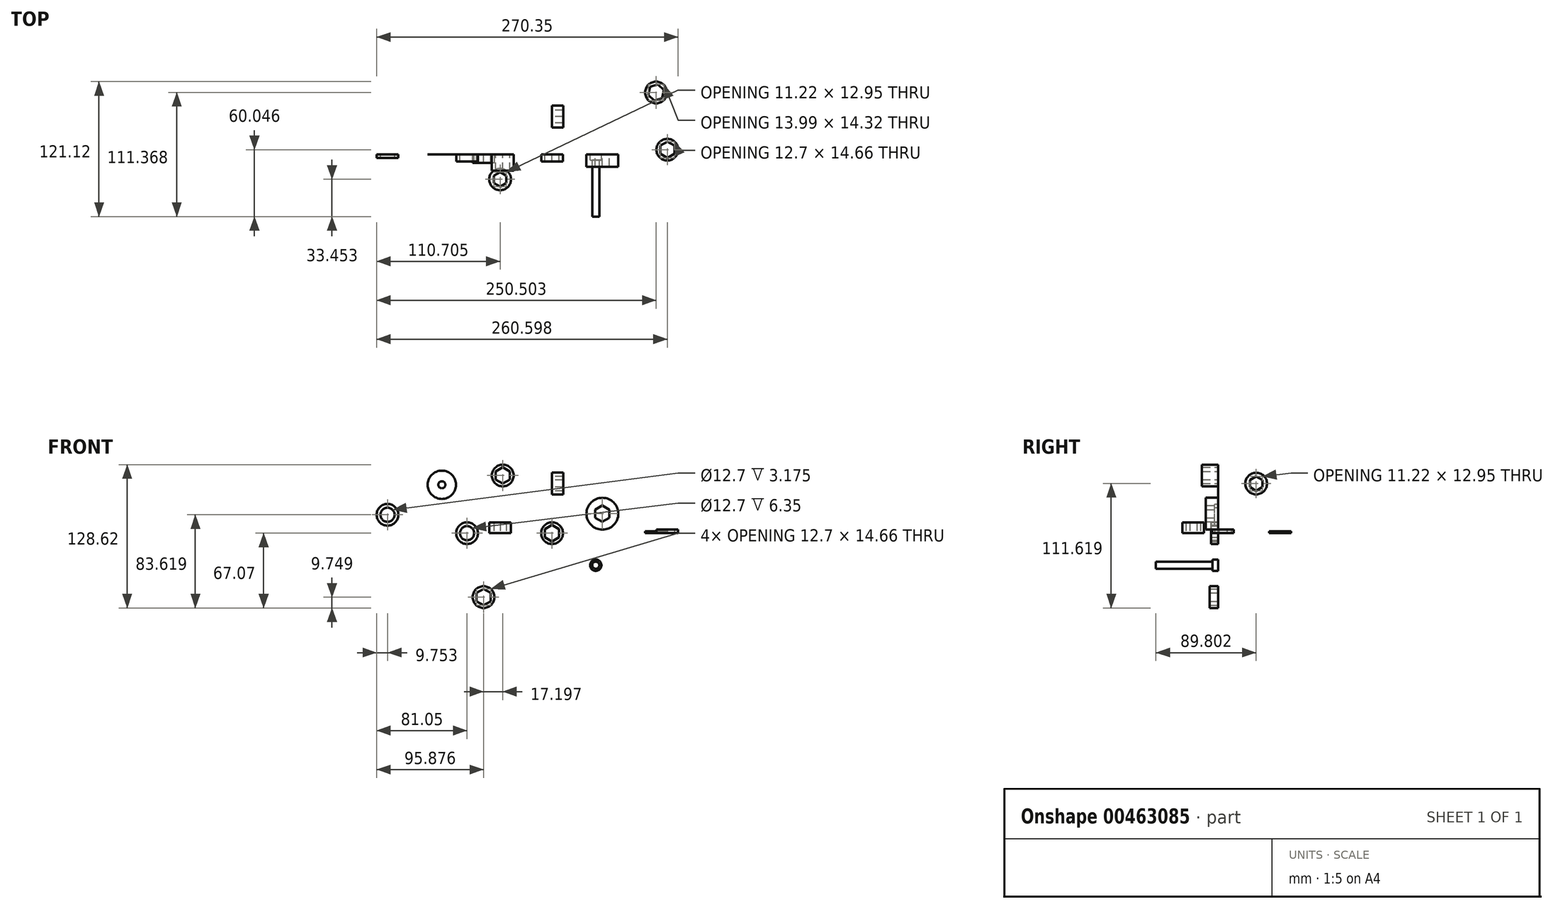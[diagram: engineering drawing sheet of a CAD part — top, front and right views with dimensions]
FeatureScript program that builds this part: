
annotation { "Feature Type Name" : "Feature", "Feature Type Description" : "" }
export const myFeature = defineFeature(function(context is Context, id is Id, definition is map)
    precondition{}
    {
        {
            var Q0;
            Q0=qCreatedBy(makeId("Front.planeOp"),FACE);
            var sketch = newSketch(context, id + "F0", { "sketchPlane" : qUnion([Q0])});
            skCircle(sketch, "E0.cCircle", {"center": v(0, 0) * mm, "radius": 7.33 * mm, "construction": true});
            skLineSegment(sketch, "E0.0", {"start": v(6.35, 3.67) * mm, "end": v(6.35, -3.67) * mm});
            skLineSegment(sketch, "E0.1", {"start": v(6.35, -3.67) * mm, "end": v(0, -7.33) * mm});
            skLineSegment(sketch, "E0.2", {"start": v(0, -7.33) * mm, "end": v(-6.35, -3.67) * mm});
            skLineSegment(sketch, "E0.3", {"start": v(-6.35, -3.67) * mm, "end": v(-6.35, 3.67) * mm});
            skLineSegment(sketch, "E0.4", {"start": v(-6.35, 3.67) * mm, "end": v(0, 7.33) * mm});
            skLineSegment(sketch, "E0.5", {"start": v(0, 7.33) * mm, "end": v(6.35, 3.67) * mm});
            skLineSegment(sketch, "E1", {"start": v(0, 0) * mm, "end": v(0, 7.33) * mm, "construction": true});
            skCircle(sketch, "E2", {"center": v(0, 0) * mm, "radius": 9.75 * mm});
            skLineSegment(sketch, "E3", {"start": v(0, 0) * mm, "end": v(-3.18, 5.5) * mm, "construction": true});
            skSolve(sketch);
        }
        {
            var Q0;
            Q0=makeQuery(id+"F0.imprint","IMPRINT",FACE,{"disambiguationData":[TD([[makeQuery(id+"F0.imprint","IMPRINT",EDGE,{"derivedFrom":sQuery(id+"F0.wireOp",EDGE,"E0.0")}),1.0]])]});
            extrude(context, id + "F1", {"entities" : qUnion([Q0]), "depth" : 6.35 * mm});
        }
        {
            var Q0;
            Q0=qCreatedBy(makeId("Top.planeOp"),FACE);
            var sketch = newSketch(context, id + "F2", { "sketchPlane" : qUnion([Q0])});
            skCircle(sketch, "E4.cCircle", {"center": v(-46.55, -22.43) * mm, "radius": 6.48 * mm, "construction": true});
            skLineSegment(sketch, "E4.0", {"start": v(-40.94, -19.19) * mm, "end": v(-40.94, -25.67) * mm});
            skLineSegment(sketch, "E4.1", {"start": v(-40.94, -25.67) * mm, "end": v(-46.55, -28.9) * mm});
            skLineSegment(sketch, "E4.2", {"start": v(-46.55, -28.9) * mm, "end": v(-52.15, -25.67) * mm});
            skLineSegment(sketch, "E4.3", {"start": v(-52.15, -25.67) * mm, "end": v(-52.15, -19.19) * mm});
            skLineSegment(sketch, "E4.4", {"start": v(-52.15, -19.19) * mm, "end": v(-46.55, -15.95) * mm});
            skLineSegment(sketch, "E4.5", {"start": v(-46.55, -15.95) * mm, "end": v(-40.94, -19.19) * mm});
            skLineSegment(sketch, "E5", {"start": v(-46.55, -22.43) * mm, "end": v(-46.55, -15.95) * mm, "construction": true});
            skCircle(sketch, "E6", {"center": v(-46.55, -22.43) * mm, "radius": 9.75 * mm});
            skSolve(sketch);
        }
        {
            var Q0;
            Q0=makeQuery(id+"F2.imprint","IMPRINT",FACE,{"disambiguationData":[TD([[makeQuery(id+"F2.imprint","IMPRINT",EDGE,{"derivedFrom":sQuery(id+"F2.wireOp",EDGE,"E4.0")}),1.0]])]});
            extrude(context, id + "F3", {"entities" : qUnion([Q0]), "depth" : 9.52 * mm});
        }
        {
            var Q0;
            Q0=qCreatedBy(makeId("Right.planeOp"),FACE);
            var sketch = newSketch(context, id + "F4", { "sketchPlane" : qUnion([Q0])});
            skCircle(sketch, "E7.cCircle", {"center": v(33.92, 44.55) * mm, "radius": 6.48 * mm, "construction": true});
            skLineSegment(sketch, "E7.0", {"start": v(39.53, 47.79) * mm, "end": v(39.53, 41.31) * mm});
            skLineSegment(sketch, "E7.1", {"start": v(39.53, 41.31) * mm, "end": v(33.92, 38.07) * mm});
            skLineSegment(sketch, "E7.2", {"start": v(33.92, 38.07) * mm, "end": v(28.31, 41.31) * mm});
            skLineSegment(sketch, "E7.3", {"start": v(28.31, 41.31) * mm, "end": v(28.31, 47.79) * mm});
            skLineSegment(sketch, "E7.4", {"start": v(28.31, 47.79) * mm, "end": v(33.92, 51.03) * mm});
            skLineSegment(sketch, "E7.5", {"start": v(33.92, 51.03) * mm, "end": v(39.53, 47.79) * mm});
            skLineSegment(sketch, "E8", {"start": v(33.92, 44.55) * mm, "end": v(33.92, 51.03) * mm, "construction": true});
            skCircle(sketch, "E9", {"center": v(33.92, 44.55) * mm, "radius": 9.75 * mm});
            skSolve(sketch);
        }
        {
            var Q0;
            Q0=makeQuery(id+"F4.imprint","IMPRINT",FACE,{"disambiguationData":[TD([[makeQuery(id+"F4.imprint","IMPRINT",EDGE,{"derivedFrom":sQuery(id+"F4.wireOp",EDGE,"E7.0")}),1.0]])]});
            extrude(context, id + "F5", {"entities" : qUnion([Q0]), "depth" : 10.16 * mm});
        }
        {
            var Q0;
            Q0=qCreatedBy(makeId("Top.planeOp"),FACE);
            var sketch = newSketch(context, id + "F6", { "sketchPlane" : qUnion([Q0])});
            skCircle(sketch, "E10.cCircle", {"center": v(103.35, 4.17) * mm, "radius": 7.33 * mm, "construction": true});
            skLineSegment(sketch, "E10.0", {"start": v(109.7, 7.83) * mm, "end": v(109.7, 0.5) * mm});
            skLineSegment(sketch, "E10.1", {"start": v(109.7, 0.5) * mm, "end": v(103.35, -3.17) * mm});
            skLineSegment(sketch, "E10.2", {"start": v(103.35, -3.17) * mm, "end": v(97, 0.5) * mm});
            skLineSegment(sketch, "E10.3", {"start": v(97, 0.5) * mm, "end": v(97, 7.83) * mm});
            skLineSegment(sketch, "E10.4", {"start": v(97, 7.83) * mm, "end": v(103.35, 11.5) * mm});
            skLineSegment(sketch, "E10.5", {"start": v(103.35, 11.5) * mm, "end": v(109.7, 7.83) * mm});
            skLineSegment(sketch, "E11", {"start": v(103.35, 4.17) * mm, "end": v(103.35, 11.5) * mm, "construction": true});
            skCircle(sketch, "E12", {"center": v(103.35, 4.17) * mm, "radius": 9.75 * mm});
            skLineSegment(sketch, "E13", {"start": v(103.35, 4.17) * mm, "end": v(100.17, 9.67) * mm, "construction": true});
            skSolve(sketch);
        }
        {
            var Q0;
            Q0=makeQuery(id+"F6.imprint","IMPRINT",FACE,{"disambiguationData":[TD([[makeQuery(id+"F6.imprint","IMPRINT",EDGE,{"derivedFrom":sQuery(id+"F6.wireOp",EDGE,"E10.0")}),1.0]])]});
            extrude(context, id + "F7", {"entities" : qUnion([Q0]), "depth" : 3.17 * mm});
        }
        {
            var Q0;
            Q0=qCreatedBy(makeId("Front.planeOp"),FACE);
            var sketch = newSketch(context, id + "F8", { "sketchPlane" : qUnion([Q0])});
            skCircle(sketch, "E14", {"center": v(-76.2, 0) * mm, "radius": 9.75 * mm});
            skCircle(sketch, "E15", {"center": v(-76.2, 0) * mm, "radius": 6.35 * mm});
            skLineSegment(sketch, "E16", {"start": v(-76.2, 0) * mm, "end": v(0, 0) * mm, "construction": true});
            skSolve(sketch);
        }
        {
            var Q0;
            Q0=makeQuery(id+"F8.imprint","IMPRINT",FACE,{"disambiguationData":[TD([[makeQuery(id+"F8.imprint","IMPRINT",EDGE,{"derivedFrom":sQuery(id+"F8.wireOp",EDGE,"E14")}),1.0]])]});
            extrude(context, id + "F9", {"entities" : qUnion([Q0]), "depth" : 6.35 * mm});
        }
        {
            var Q0;
            Q0=qCreatedBy(makeId("Top.planeOp"),FACE);
            var sketch = newSketch(context, id + "F10", { "sketchPlane" : qUnion([Q0])});
            skCircle(sketch, "E17.cCircle", {"center": v(93.25, 55.49) * mm, "radius": 7.33 * mm, "construction": true});
            skLineSegment(sketch, "E17.0", {"start": v(100.25, 57.69) * mm, "end": v(98.66, 50.53) * mm});
            skLineSegment(sketch, "E17.1", {"start": v(98.66, 50.53) * mm, "end": v(91.66, 48.33) * mm});
            skLineSegment(sketch, "E17.2", {"start": v(91.66, 48.33) * mm, "end": v(86.26, 53.29) * mm});
            skLineSegment(sketch, "E17.3", {"start": v(86.26, 53.29) * mm, "end": v(87.85, 60.44) * mm});
            skLineSegment(sketch, "E17.4", {"start": v(87.85, 60.44) * mm, "end": v(94.84, 62.65) * mm});
            skLineSegment(sketch, "E17.5", {"start": v(94.84, 62.65) * mm, "end": v(100.25, 57.69) * mm});
            skCircle(sketch, "E18", {"center": v(93.25, 55.49) * mm, "radius": 9.75 * mm});
            skSolve(sketch);
        }
        {
            var Q0;
            Q0=makeQuery(id+"F10.imprint","IMPRINT",FACE,{"disambiguationData":[TD([[makeQuery(id+"F10.imprint","IMPRINT",EDGE,{"derivedFrom":sQuery(id+"F10.wireOp",EDGE,"E17.0")}),1.0]])]});
            extrude(context, id + "F11", {"entities" : qUnion([Q0]), "depth" : 1.59 * mm});
        }
        {
            var Q0;
            Q0=qCreatedBy(makeId("Front.planeOp"),FACE);
            var sketch = newSketch(context, id + "F12", { "sketchPlane" : qUnion([Q0])});
            skCircle(sketch, "E19", {"center": v(-147.5, 16.55) * mm, "radius": 9.75 * mm});
            skCircle(sketch, "E20", {"center": v(-147.5, 16.55) * mm, "radius": 6.35 * mm});
            skSolve(sketch);
        }
        {
            var Q0;
            Q0=makeQuery(id+"F12.imprint","IMPRINT",FACE,{"disambiguationData":[TD([[makeQuery(id+"F12.imprint","IMPRINT",EDGE,{"derivedFrom":sQuery(id+"F12.wireOp",EDGE,"E19")}),1.0]])]});
            extrude(context, id + "F13", {"entities" : qUnion([Q0]), "depth" : 3.17 * mm});
        }
        {
            var Q0;
            Q0=qCreatedBy(makeId("Front.planeOp"),FACE);
            var sketch = newSketch(context, id + "F14", { "sketchPlane" : qUnion([Q0])});
            skCircle(sketch, "E21.cCircle", {"center": v(45.16, 17.5) * mm, "radius": 6.35 * mm, "construction": true});
            skLineSegment(sketch, "E21.0", {"start": v(51.51, 21.16) * mm, "end": v(51.51, 13.83) * mm});
            skLineSegment(sketch, "E21.1", {"start": v(51.51, 13.83) * mm, "end": v(45.16, 10.16) * mm});
            skLineSegment(sketch, "E21.2", {"start": v(45.16, 10.16) * mm, "end": v(38.81, 13.83) * mm});
            skLineSegment(sketch, "E21.3", {"start": v(38.81, 13.83) * mm, "end": v(38.81, 21.16) * mm});
            skLineSegment(sketch, "E21.4", {"start": v(38.81, 21.16) * mm, "end": v(45.16, 24.83) * mm});
            skLineSegment(sketch, "E21.5", {"start": v(45.16, 24.83) * mm, "end": v(51.51, 21.16) * mm});
            skPoint(sketch, "E21.0.midPoint", {"position": v(51.51, 17.5) * mm});
            skCircle(sketch, "E22", {"center": v(45.16, 17.5) * mm, "radius": 14.29 * mm});
            skSolve(sketch);
        }
        {
            var Q0;
            Q0=makeQuery(id+"F14.imprint","IMPRINT",FACE,{"disambiguationData":[TD([[makeQuery(id+"F14.imprint","IMPRINT",EDGE,{"derivedFrom":sQuery(id+"F14.wireOp",EDGE,"E21.0")}),1.0]])]});
            extrude(context, id + "F15", {"entities" : qUnion([Q0]), "depth" : 11.1 * mm});
        }
        {
            var Q0;
            Q0=qCreatedBy(makeId("Front.planeOp"),FACE);
            var sketch = newSketch(context, id + "F16", { "sketchPlane" : qUnion([Q0])});
            skCircle(sketch, "E23.cCircle", {"center": v(-44.18, 51.8) * mm, "radius": 6.35 * mm, "construction": true});
            skLineSegment(sketch, "E23.0", {"start": v(-37.83, 55.46) * mm, "end": v(-37.83, 48.13) * mm});
            skLineSegment(sketch, "E23.1", {"start": v(-37.83, 48.13) * mm, "end": v(-44.18, 44.46) * mm});
            skLineSegment(sketch, "E23.2", {"start": v(-44.18, 44.46) * mm, "end": v(-50.53, 48.13) * mm});
            skLineSegment(sketch, "E23.3", {"start": v(-50.53, 48.13) * mm, "end": v(-50.53, 55.46) * mm});
            skLineSegment(sketch, "E23.4", {"start": v(-50.53, 55.46) * mm, "end": v(-44.18, 59.13) * mm});
            skLineSegment(sketch, "E23.5", {"start": v(-44.18, 59.13) * mm, "end": v(-37.83, 55.46) * mm});
            skPoint(sketch, "E23.0.midPoint", {"position": v(-37.83, 51.8) * mm});
            skCircle(sketch, "E24", {"center": v(-44.18, 51.8) * mm, "radius": 9.75 * mm});
            skSolve(sketch);
        }
        {
            var Q0;
            Q0=makeQuery(id+"F16.imprint","IMPRINT",FACE,{"disambiguationData":[TD([[makeQuery(id+"F16.imprint","IMPRINT",EDGE,{"derivedFrom":sQuery(id+"F16.wireOp",EDGE,"E23.0")}),1.0]])]});
            extrude(context, id + "F17", {"entities" : qUnion([Q0]), "depth" : 14.71 * mm});
        }
        {
            var Q0;
            Q0=qCreatedBy(makeId("Front.planeOp"),FACE);
            var sketch = newSketch(context, id + "F18", { "sketchPlane" : qUnion([Q0])});
            skCircle(sketch, "E25", {"center": v(-98.78, 43.46) * mm, "radius": 3.18 * mm});
            skCircle(sketch, "E26", {"center": v(-98.78, 43.46) * mm, "radius": 12.7 * mm});
            skSolve(sketch);
        }
        {
            var Q0;
            Q0=qCreatedBy(makeId("Front.planeOp"),FACE);
            var sketch = newSketch(context, id + "F19", { "sketchPlane" : qUnion([Q0])});
            skCircle(sketch, "E27.cCircle", {"center": v(-61.37, -57.32) * mm, "radius": 7.33 * mm, "construction": true});
            skLineSegment(sketch, "E27.0", {"start": v(-55.02, -53.65) * mm, "end": v(-55.02, -60.99) * mm});
            skLineSegment(sketch, "E27.1", {"start": v(-55.02, -60.99) * mm, "end": v(-61.37, -64.65) * mm});
            skLineSegment(sketch, "E27.2", {"start": v(-61.37, -64.65) * mm, "end": v(-67.72, -60.99) * mm});
            skLineSegment(sketch, "E27.3", {"start": v(-67.72, -60.99) * mm, "end": v(-67.72, -53.65) * mm});
            skLineSegment(sketch, "E27.4", {"start": v(-67.72, -53.65) * mm, "end": v(-61.37, -49.99) * mm});
            skLineSegment(sketch, "E27.5", {"start": v(-61.37, -49.99) * mm, "end": v(-55.02, -53.65) * mm});
            skLineSegment(sketch, "E28", {"start": v(-61.37, -57.32) * mm, "end": v(-61.37, -49.99) * mm, "construction": true});
            skCircle(sketch, "E29", {"center": v(-61.37, -57.32) * mm, "radius": 9.75 * mm});
            skLineSegment(sketch, "E30", {"start": v(-61.37, -57.32) * mm, "end": v(-64.55, -51.82) * mm, "construction": true});
            skSolve(sketch);
        }
        {
            var Q0;
            Q0=makeQuery(id+"F18.imprint","IMPRINT",FACE,{"disambiguationData":[TD([[makeQuery(id+"F18.imprint","IMPRINT",EDGE,{"derivedFrom":sQuery(id+"F18.wireOp",EDGE,"E25")}),-1.0]])]});
            extrude(context, id + "F20", {"entities" : qUnion([Q0]), "depth" : 1 / 406.4 * mm});
        }
        {
            var Q0;
            Q0=makeQuery(id+"F19.imprint","IMPRINT",FACE,{"disambiguationData":[TD([[makeQuery(id+"F19.imprint","IMPRINT",EDGE,{"derivedFrom":sQuery(id+"F19.wireOp",EDGE,"E27.0")}),1.0]])]});
            extrude(context, id + "F21", {"entities" : qUnion([Q0]), "depth" : 7.62 * mm});
        }
        {
            var Q0;
            Q0=qCreatedBy(makeId("Front.planeOp"),FACE);
            var sketch = newSketch(context, id + "F22", { "sketchPlane" : qUnion([Q0])});
            skCircle(sketch, "E31", {"center": v(39.18, -28.69) * mm, "radius": 5.08 * mm});
            skSolve(sketch);
        }
        {
            var Q0;
            Q0=makeQuery(id+"F22.imprint","IMPRINT",FACE,{"disambiguationData":[TD([[makeQuery(id+"F22.imprint","IMPRINT",EDGE,{"derivedFrom":sQuery(id+"F22.wireOp",EDGE,"E31")}),1.0]])]});
            extrude(context, id + "F23", {"entities" : qUnion([Q0]), "depth" : 5.08 * mm});
        }
        {
            var Q0;
            Q0=makeQuery(id+"F23.opExtrude","CAP_FACE",FACE,{"disambiguationData":[OSD([sQuery(id+"F22.wireOp",EDGE,"E31")])],"isStart":false});
            var sketch = newSketch(context, id + "F24", { "sketchPlane" : qUnion([Q0])});
            skCircle(sketch, "E32", {"center": v(39.18, -28.69) * mm, "radius": 3.18 * mm});
            skSolve(sketch);
        }
        {
            var Q0;
            Q0=makeQuery(id+"F24.imprint","IMPRINT",FACE,{"disambiguationData":[TD([[makeQuery(id+"F24.imprint","IMPRINT",EDGE,{"derivedFrom":sQuery(id+"F24.wireOp",EDGE,"E32")}),1.0]])]});
            extrude(context, id + "F25", {"entities" : qUnion([Q0]), "operationType" : NewBodyOperationType.ADD, "depth" : 50.8 * mm});
        }
    });
